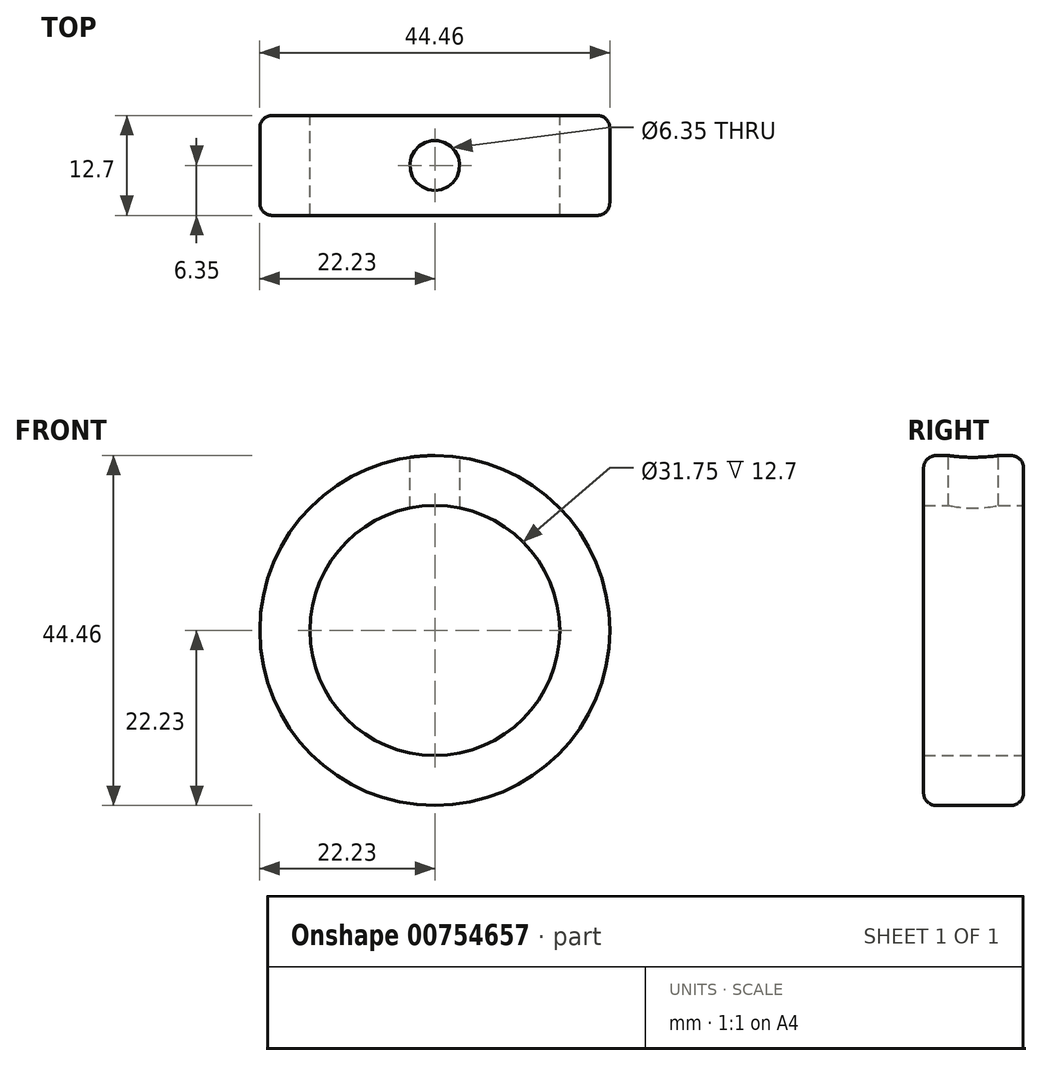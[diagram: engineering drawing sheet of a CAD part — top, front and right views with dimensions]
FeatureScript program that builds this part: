
annotation { "Feature Type Name" : "Feature", "Feature Type Description" : "" }
export const myFeature = defineFeature(function(context is Context, id is Id, definition is map)
    precondition{}
    {
        {
            var Q0;
            Q0=qCreatedBy(makeId("Front.planeOp"),FACE);
            var sketch = newSketch(context, id + "F0", { "sketchPlane" : qUnion([Q0])});
            skCircle(sketch, "E0", {"center": v(0, 0) * mm, "radius": 15.88 * mm});
            skCircle(sketch, "E1", {"center": v(0, 0) * mm, "radius": 22.23 * mm});
            skSolve(sketch);
        }
        {
            var Q0;
            Q0=makeQuery(id+"F0.imprint","IMPRINT",FACE,{"disambiguationData":[TD([[makeQuery(id+"F0.imprint","IMPRINT",EDGE,{"derivedFrom":sQuery(id+"F0.wireOp",EDGE,"E0")}),-1.0]])]});
            extrude(context, id + "F1", {"entities" : qUnion([Q0]), "depth" : 12.7 * mm, "offsetDistance" : 25.4 * mm});
        }
        {
            var Q0;
            Q0=qCreatedBy(makeId("Top.planeOp"),FACE);
            cPlane(context, id + "F2", {"entities" : qUnion([Q0]), "cplaneType" : CPlaneType.OFFSET, "offset" : 23.37 * mm, "width" : 152.4 * mm, "height" : 152.4 * mm});
        }
        {
            var Q0;
            Q0=qCreatedBy(id+"F2.planeOp",FACE);
            var sketch = newSketch(context, id + "F3", { "sketchPlane" : qUnion([Q0])});
            skCircle(sketch, "E2", {"center": v(0, -6.35) * mm, "radius": 3.18 * mm});
            skLineSegment(sketch, "E3", {"start": v(0, 0) * mm, "end": v(0, -6.35) * mm, "construction": true});
            skSolve(sketch);
        }
        {
            var Q0;
            Q0 = qSketchRegion(id + "F3", true);
            extrude(context, id + "F4", {"entities" : qUnion([Q0]), "operationType" : NewBodyOperationType.REMOVE, "oppositeDirection" : true, "depth" : 12.7 * mm, "offsetDistance" : 25.4 * mm});
        }
        {
            var Q0;
            Q0=makeQuery(id+"F1.opExtrude","CAP_EDGE",EDGE,{"disambiguationData":[OSD([sQuery(id+"F0.wireOp",EDGE,"E1")])],"isStart":false});
            var Q1;
            Q1=makeQuery(id+"F1.opExtrude","CAP_EDGE",EDGE,{"disambiguationData":[OSD([sQuery(id+"F0.wireOp",EDGE,"E1")])],"isStart":true});
            fillet(context, id + "F5", {"entities" : qUnion([Q0, Q1]), "radius" : 1.59 * mm, "tangentPropagation" : true, "allowEdgeOverflow" : false});
        }
    });
